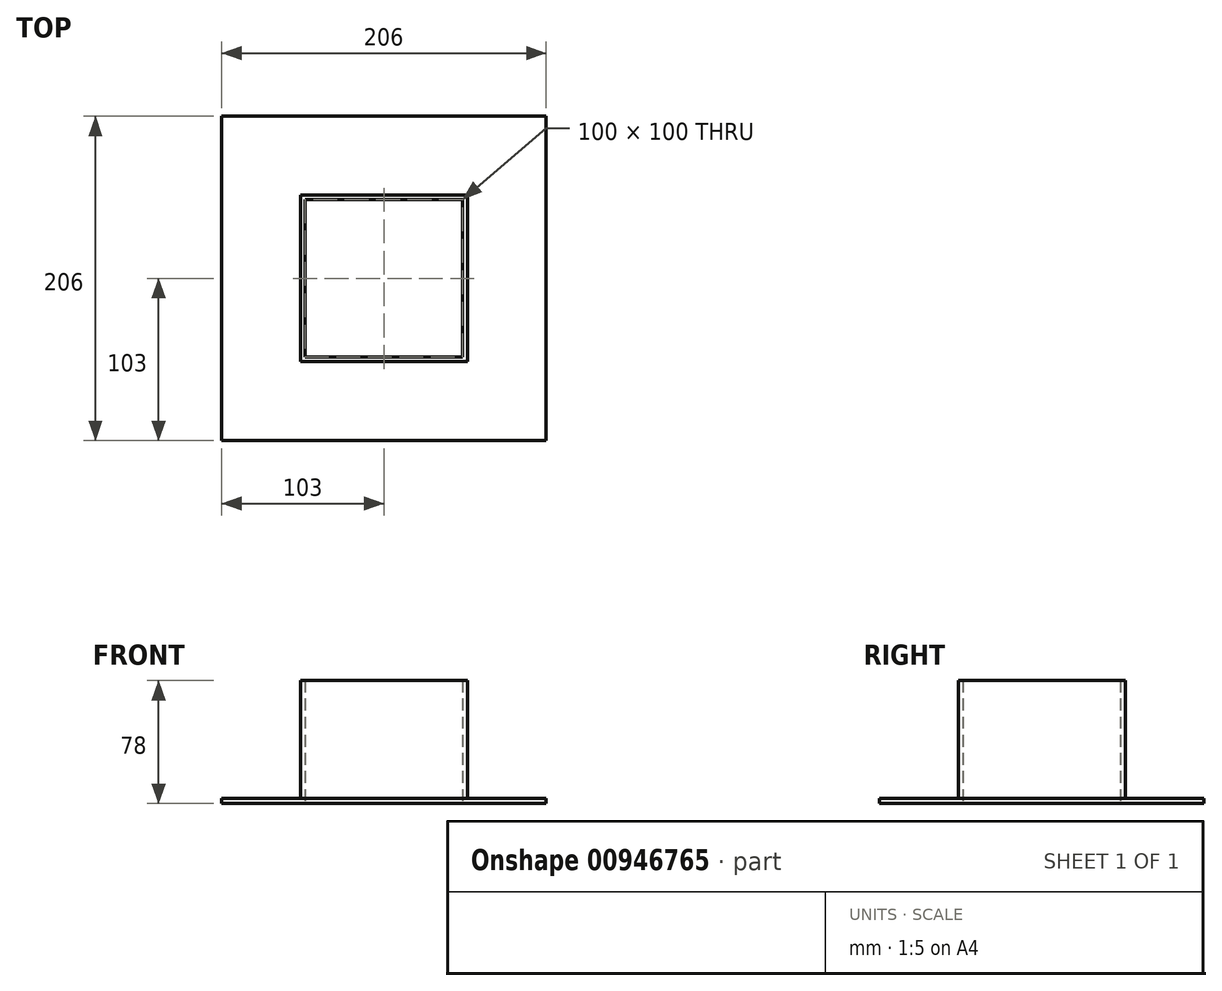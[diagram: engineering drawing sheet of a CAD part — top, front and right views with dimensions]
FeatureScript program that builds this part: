
annotation { "Feature Type Name" : "Feature", "Feature Type Description" : "" }
export const myFeature = defineFeature(function(context is Context, id is Id, definition is map)
    precondition{}
    {
        {
            var Q0;
            Q0=qCreatedBy(makeId("Top.planeOp"),FACE);
            var sketch = newSketch(context, id + "F0", { "sketchPlane" : qUnion([Q0])});
            skLineSegment(sketch, "E0.bottom", {"start": v(50, 50) * mm, "end": v(-50, 50) * mm});
            skLineSegment(sketch, "E0.top", {"start": v(50, -50) * mm, "end": v(-50, -50) * mm});
            skLineSegment(sketch, "E0.left", {"start": v(50, 50) * mm, "end": v(50, -50) * mm});
            skLineSegment(sketch, "E0.right", {"start": v(-50, 50) * mm, "end": v(-50, -50) * mm});
            skPoint(sketch, "E0.middle", {"position": v(0, 0) * mm});
            skLineSegment(sketch, "E1.0", {"start": v(103, 103) * mm, "end": v(-103, 103) * mm});
            skLineSegment(sketch, "E1.1", {"start": v(103, 103) * mm, "end": v(103, -103) * mm});
            skLineSegment(sketch, "E1.2", {"start": v(103, -103) * mm, "end": v(-103, -103) * mm});
            skLineSegment(sketch, "E1.3", {"start": v(-103, 103) * mm, "end": v(-103, -103) * mm});
            skSolve(sketch);
        }
        {
            var Q0;
            Q0=makeQuery(id+"F0.imprint","IMPRINT",FACE,{"disambiguationData":[TD([[makeQuery(id+"F0.imprint","IMPRINT",EDGE,{"derivedFrom":sQuery(id+"F0.wireOp",EDGE,"5e6dec59-04c9-4f53-9c1f-86acaf43ab85.0")}),1.0]])]});
            var Q1;
            Q1=makeQuery(id+"F0.imprint","IMPRINT",FACE,{"disambiguationData":[TD([[makeQuery(id+"F0.imprint","IMPRINT",EDGE,{"derivedFrom":sQuery(id+"F0.wireOp",EDGE,"E0.bottom")}),-1.0]])]});
            extrude(context, id + "F1", {"entities" : qUnion([Q0, Q1]), "depth" : 3 * mm, "offsetDistance" : 25 * mm});
        }
        {
            var Q0;
            Q0=makeQuery(id+"F1.opExtrude","CAP_FACE",FACE,{"disambiguationData":[OSD([sQuery(id+"F0.wireOp",EDGE,"E0.bottom"),sQuery(id+"F0.wireOp",EDGE,"E0.top"),sQuery(id+"F0.wireOp",EDGE,"E0.left"),sQuery(id+"F0.wireOp",EDGE,"E0.right"),sQuery(id+"F0.wireOp",EDGE,"E1.0"),sQuery(id+"F0.wireOp",EDGE,"E1.1"),sQuery(id+"F0.wireOp",EDGE,"E1.2"),sQuery(id+"F0.wireOp",EDGE,"E1.3")])],"isStart":false});
            var sketch = newSketch(context, id + "F2", { "sketchPlane" : qUnion([Q0])});
            skLineSegment(sketch, "E2.0", {"start": v(50, 50) * mm, "end": v(-50, 50) * mm});
            skLineSegment(sketch, "E3.0", {"start": v(50, 50) * mm, "end": v(50, -50) * mm});
            skLineSegment(sketch, "E4.0", {"start": v(50, -50) * mm, "end": v(-50, -50) * mm});
            skLineSegment(sketch, "E5.0", {"start": v(-50, 50) * mm, "end": v(-50, -50) * mm});
            skLineSegment(sketch, "E6.0", {"start": v(53, 53) * mm, "end": v(-53, 53) * mm});
            skLineSegment(sketch, "E6.1", {"start": v(53, 53) * mm, "end": v(53, -53) * mm});
            skLineSegment(sketch, "E6.2", {"start": v(53, -53) * mm, "end": v(-53, -53) * mm});
            skLineSegment(sketch, "E6.3", {"start": v(-53, 53) * mm, "end": v(-53, -53) * mm});
            skSolve(sketch);
        }
        {
            var Q0;
            Q0=makeQuery(id+"F2.imprint","IMPRINT",FACE,{"disambiguationData":[TD([[makeQuery(id+"F2.imprint","IMPRINT",EDGE,{"derivedFrom":sQuery(id+"F2.wireOp",EDGE,"E2.0")}),-1.0]])]});
            extrude(context, id + "F3", {"entities" : qUnion([Q0]), "operationType" : NewBodyOperationType.ADD, "depth" : 75 * mm, "offsetDistance" : 25 * mm});
        }
    });
